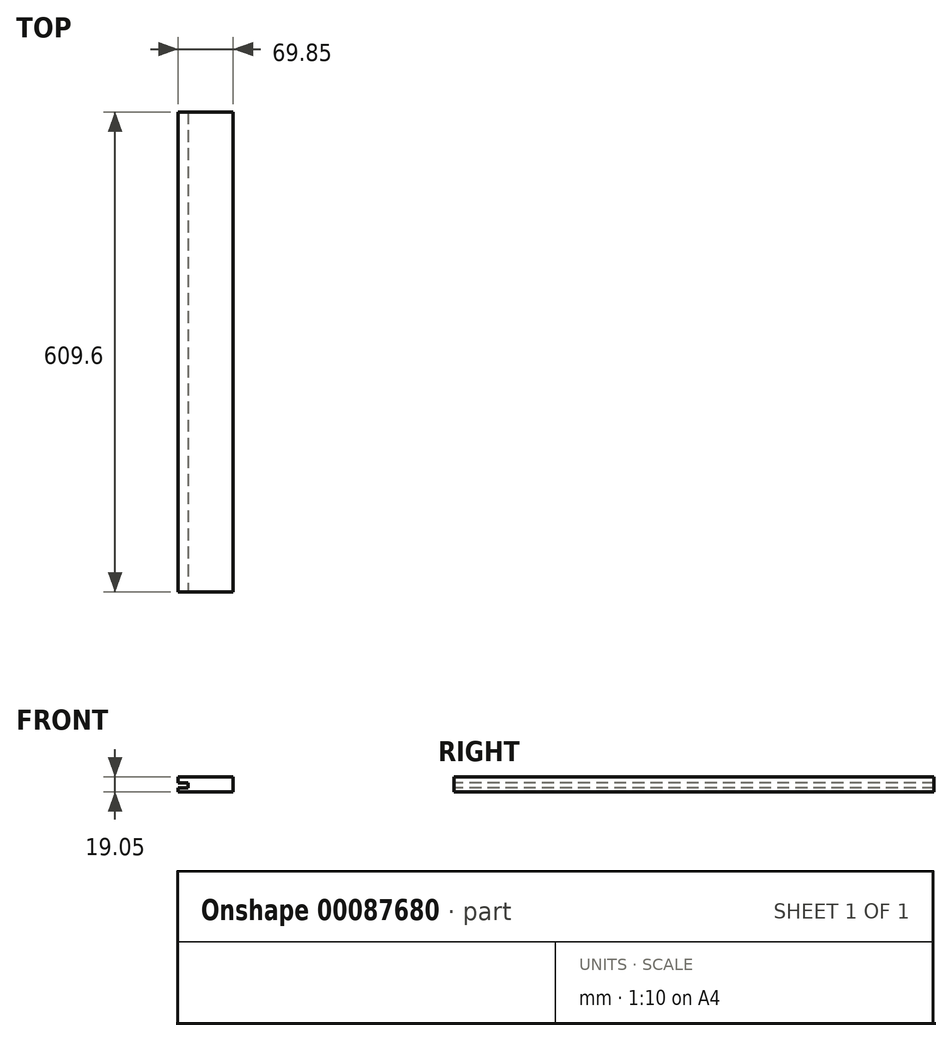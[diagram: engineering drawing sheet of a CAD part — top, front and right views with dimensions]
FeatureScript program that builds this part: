
annotation { "Feature Type Name" : "Feature", "Feature Type Description" : "" }
export const myFeature = defineFeature(function(context is Context, id is Id, definition is map)
    precondition{}
    {
        {
            var Q0;
            Q0=qCreatedBy(makeId("Front.planeOp"),FACE);
            var sketch = newSketch(context, id + "F0", { "sketchPlane" : qUnion([Q0])});
            skLineSegment(sketch, "E0.bottom", {"start": v(0, 0) * mm, "end": v(-69.85, 0) * mm});
            skLineSegment(sketch, "E0.top", {"start": v(0, 19.05) * mm, "end": v(-69.85, 19.05) * mm});
            skLineSegment(sketch, "E0.left", {"start": v(0, 0) * mm, "end": v(0, 19.05) * mm});
            skLineSegment(sketch, "E0.right", {"start": v(-69.85, 0) * mm, "end": v(-69.85, 19.05) * mm});
            skSolve(sketch);
        }
        {
            var Q0;
            Q0=makeQuery(id+"F0.imprint","IMPRINT",FACE,{"disambiguationData":[TD([[makeQuery(id+"F0.imprint","IMPRINT",EDGE,{"derivedFrom":sQuery(id+"F0.wireOp",EDGE,"E0.bottom")}),-1.0]])]});
            extrude(context, id + "F1", {"entities" : qUnion([Q0]), "depth" : 609.6 * mm});
        }
        {
            var Q0;
            Q0=makeQuery(id+"F1.opExtrude","CAP_FACE",FACE,{"disambiguationData":[OSD([sQuery(id+"F0.wireOp",EDGE,"E0.bottom"),sQuery(id+"F0.wireOp",EDGE,"E0.top"),sQuery(id+"F0.wireOp",EDGE,"E0.left"),sQuery(id+"F0.wireOp",EDGE,"E0.right")])],"isStart":false});
            var sketch = newSketch(context, id + "F2", { "sketchPlane" : qUnion([Q0])});
            skLineSegment(sketch, "E1.bottom", {"start": v(-69.85, 11.43) * mm, "end": v(-57.15, 11.43) * mm});
            skLineSegment(sketch, "E1.top", {"start": v(-69.85, 5.08) * mm, "end": v(-57.15, 5.08) * mm});
            skLineSegment(sketch, "E1.left", {"start": v(-69.85, 11.43) * mm, "end": v(-69.85, 5.08) * mm});
            skLineSegment(sketch, "E1.right", {"start": v(-57.15, 11.43) * mm, "end": v(-57.15, 5.08) * mm});
            skSolve(sketch);
        }
        {
            var Q0;
            Q0 = qSketchRegion(id + "F2", true);
            extrude(context, id + "F3", {"entities" : qUnion([Q0]), "operationType" : NewBodyOperationType.REMOVE, "endBound" : BoundingType.THROUGH_ALL, "oppositeDirection" : true, "depth" : 25.4 * mm});
        }
    });
